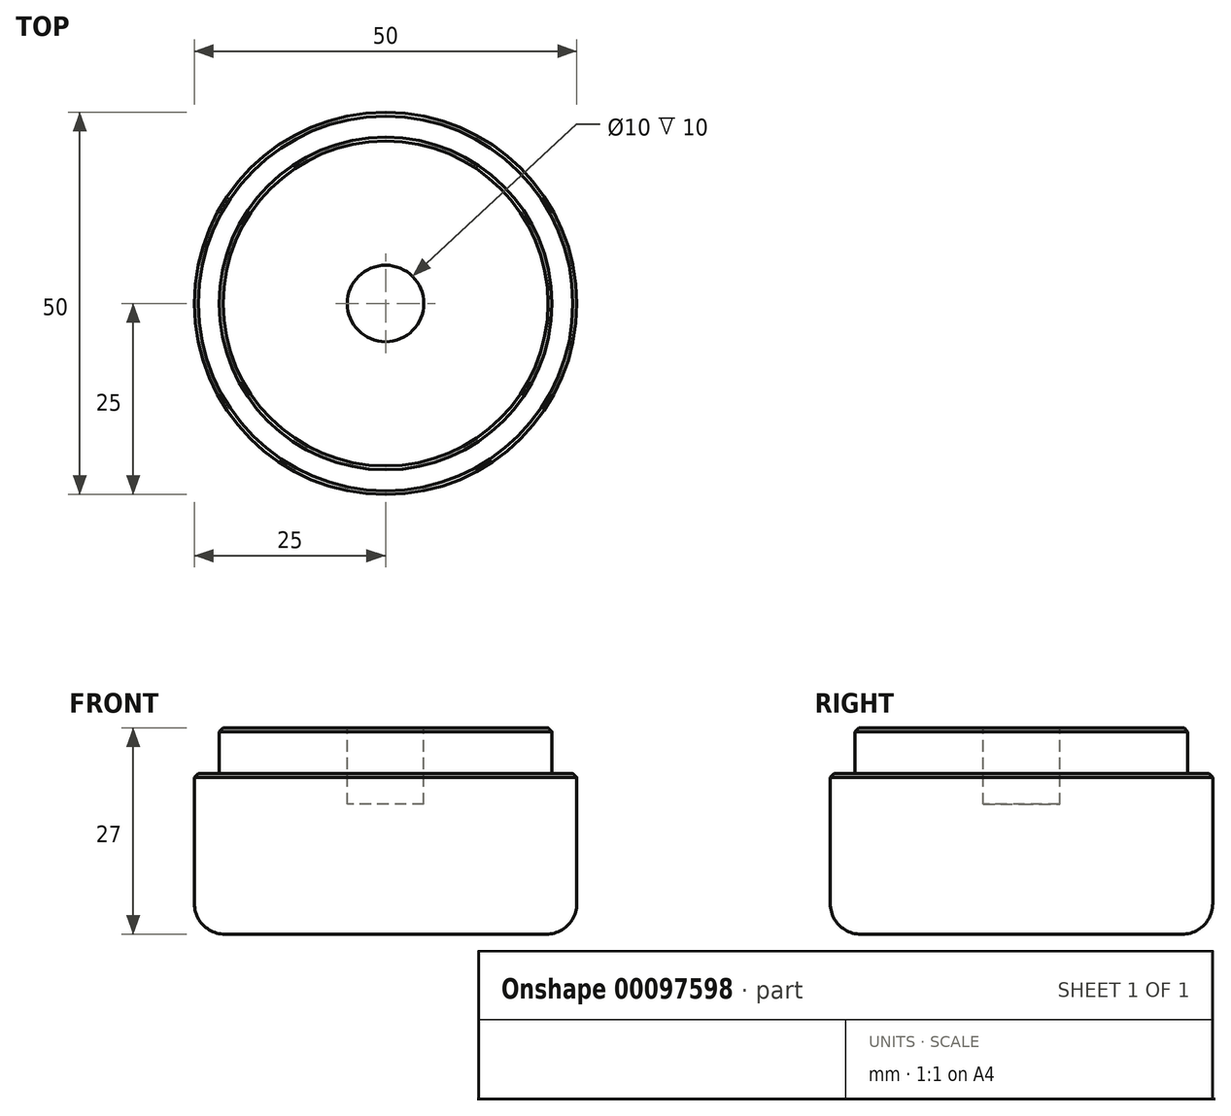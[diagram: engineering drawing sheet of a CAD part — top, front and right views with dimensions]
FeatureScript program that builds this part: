
annotation { "Feature Type Name" : "Feature", "Feature Type Description" : "" }
export const myFeature = defineFeature(function(context is Context, id is Id, definition is map)
    precondition{}
    {
        {
            var Q0;
            Q0=qCreatedBy(makeId("Top.planeOp"),FACE);
            var sketch = newSketch(context, id + "F0", { "sketchPlane" : qUnion([Q0])});
            skCircle(sketch, "E0", {"center": v(0, 0) * mm, "radius": 25 * mm});
            skSolve(sketch);
        }
        {
            var Q0;
            Q0 = qSketchRegion(id + "F0", true);
            extrude(context, id + "F1", {"entities" : qUnion([Q0]), "depth" : 21 * mm, "offsetDistance" : 25 * mm});
        }
        {
            var Q0;
            Q0=makeQuery(id+"F1.opExtrude","CAP_FACE",FACE,{"disambiguationData":[OSD([sQuery(id+"F0.wireOp",EDGE,"E0")])],"isStart":false});
            var sketch = newSketch(context, id + "F2", { "sketchPlane" : qUnion([Q0])});
            skCircle(sketch, "E1", {"center": v(0, 0) * mm, "radius": 21.75 * mm});
            skSolve(sketch);
        }
        {
            var Q0;
            Q0 = qSketchRegion(id + "F2", true);
            extrude(context, id + "F3", {"entities" : qUnion([Q0]), "operationType" : NewBodyOperationType.ADD, "depth" : 6 * mm, "offsetDistance" : 25 * mm});
        }
        {
            var Q0;
            Q0=makeQuery(id+"F3.opExtrude","CAP_FACE",FACE,{"disambiguationData":[OSD([sQuery(id+"F2.wireOp",EDGE,"E1")])],"isStart":false});
            var sketch = newSketch(context, id + "F4", { "sketchPlane" : qUnion([Q0])});
            skCircle(sketch, "E2", {"center": v(0, 0) * mm, "radius": 5 * mm});
            skSolve(sketch);
        }
        {
            var Q0;
            Q0 = qSketchRegion(id + "F4", true);
            extrude(context, id + "F5", {"entities" : qUnion([Q0]), "operationType" : NewBodyOperationType.REMOVE, "oppositeDirection" : true, "depth" : 10 * mm, "offsetDistance" : 25 * mm});
        }
        {
            var Q0;
            Q0=makeQuery(id+"F3.opExtrude","CAP_EDGE",EDGE,{"disambiguationData":[OSD([sQuery(id+"F2.wireOp",EDGE,"E1")])],"isStart":false});
            var Q1;
            Q1=makeQuery(id+"F1.opExtrude","CAP_EDGE",EDGE,{"disambiguationData":[OSD([sQuery(id+"F0.wireOp",EDGE,"E0")])],"isStart":false});
            chamfer(context, id + "F6", {"entities" : qUnion([Q0, Q1]), "width" : 0.5 * mm, "tangentPropagation" : true});
        }
        {
            var Q0;
            Q0=makeQuery(id+"F1.opExtrude","CAP_EDGE",EDGE,{"disambiguationData":[OSD([sQuery(id+"F0.wireOp",EDGE,"E0")])],"isStart":true});
            fillet(context, id + "F7", {"entities" : qUnion([Q0]), "tangentPropagation" : true, "radius" : 4 * mm, "defaultsChanged" : true, "vertexSettings" : [], "allowEdgeOverflow" : false});
        }
    });
